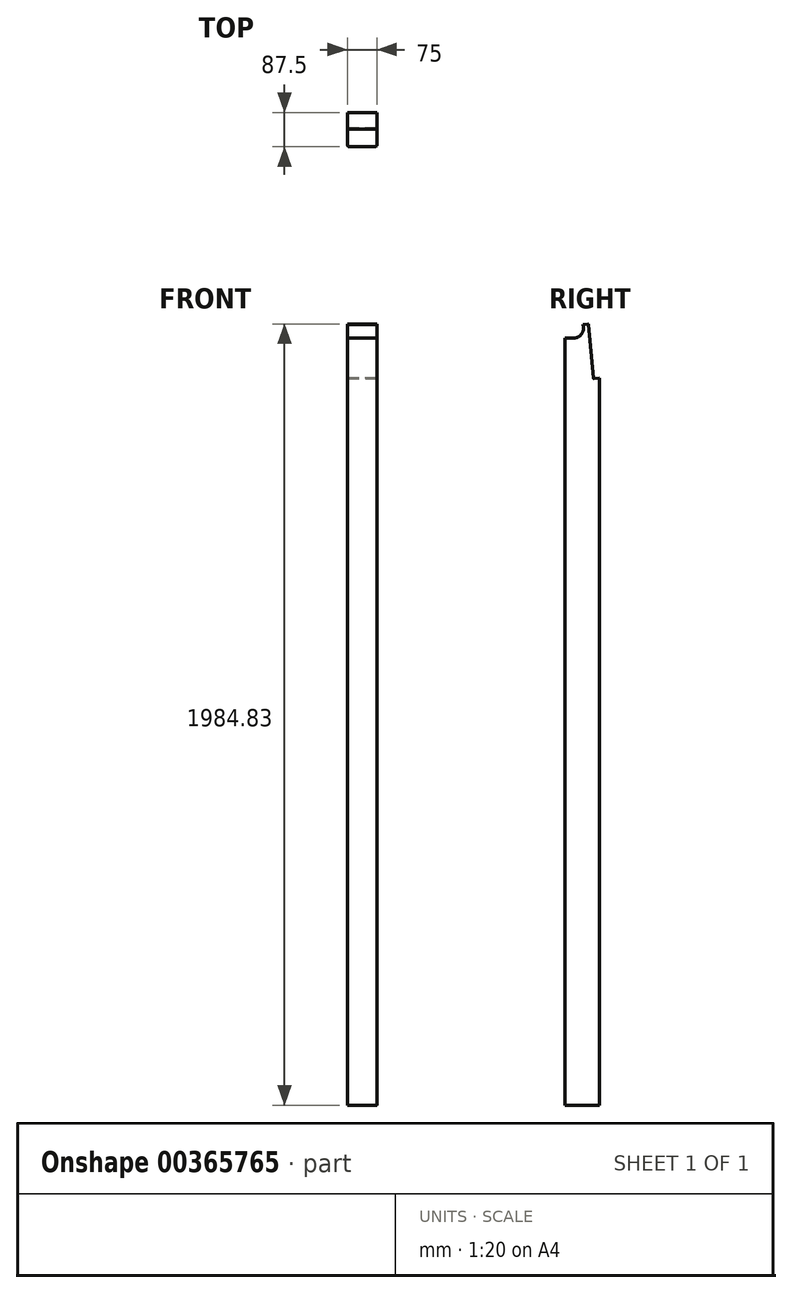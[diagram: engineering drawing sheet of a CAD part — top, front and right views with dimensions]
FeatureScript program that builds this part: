
annotation { "Feature Type Name" : "Feature", "Feature Type Description" : "" }
export const myFeature = defineFeature(function(context is Context, id is Id, definition is map)
    precondition{}
    {
        {
            var Q0;
            Q0=qCreatedBy(makeId("Top.planeOp"),FACE);
            var sketch = newSketch(context, id + "F0", { "sketchPlane" : qUnion([Q0])});
            skLineSegment(sketch, "E0.bottom", {"start": v(-37.5, 43.75) * mm, "end": v(37.5, 43.75) * mm});
            skLineSegment(sketch, "E0.top", {"start": v(-37.5, -43.75) * mm, "end": v(37.5, -43.75) * mm});
            skLineSegment(sketch, "E0.left", {"start": v(-37.5, 43.75) * mm, "end": v(-37.5, -43.75) * mm});
            skLineSegment(sketch, "E0.right", {"start": v(37.5, 43.75) * mm, "end": v(37.5, -43.75) * mm});
            skPoint(sketch, "E0.middle", {"position": v(0, 0) * mm});
            skSolve(sketch);
        }
        {
            var Q0;
            Q0=makeQuery(id+"F0.imprint","IMPRINT",FACE,{"disambiguationData":[TD([[makeQuery(id+"F0.imprint","IMPRINT",EDGE,{"derivedFrom":sQuery(id+"F0.wireOp",EDGE,"E0.bottom")}),-1.0]])]});
            extrude(context, id + "F1", {"entities" : qUnion([Q0]), "depth" : 2000 * mm});
        }
        {
            var Q0;
            Q0=makeQuery(id+"F1.opExtrude","SWEPT_EDGE",EDGE,{"disambiguationData":[OSD([sQuery(id+"F0.wireOp",EDGE,"E0.top"),sQuery(id+"F0.wireOp",EDGE,"E0.left")])]});
            var Q1;
            Q1=makeQuery(id+"F1.opExtrude","SWEPT_EDGE",EDGE,{"disambiguationData":[OSD([sQuery(id+"F0.wireOp",EDGE,"E0.top"),sQuery(id+"F0.wireOp",EDGE,"E0.right")])]});
            fillet(context, id + "F2", {"entities" : qUnion([Q0, Q1]), "radius" : 5 * mm, "tangentPropagation" : true, "allowEdgeOverflow" : false});
        }
        {
            var Q0;
            Q0=makeQuery(id+"F1.opExtrude","SWEPT_FACE",FACE,{"disambiguationData":[OSD([sQuery(id+"F0.wireOp",EDGE,"E0.left")])]});
            var sketch = newSketch(context, id + "F3", { "sketchPlane" : qUnion([Q0])});
            skLineSegment(sketch, "E1", {"start": v(-16.6, 1985) * mm, "end": v(-28.8, 1845.53) * mm});
            skLineSegment(sketch, "E2", {"start": v(-28.8, 1845.53) * mm, "end": v(-43.75, 1846.84) * mm});
            skLineSegment(sketch, "E3", {"start": v(-43.75, 1846.84) * mm, "end": v(-43.75, 2000) * mm});
            skLineSegment(sketch, "E4", {"start": v(-43.75, 2000) * mm, "end": v(43.75, 2000) * mm});
            skLineSegment(sketch, "E5", {"start": v(21.25, 1949) * mm, "end": v(43.75, 1949) * mm});
            skLineSegment(sketch, "E6", {"start": v(43.75, 1949) * mm, "end": v(43.75, 2000) * mm});
            skArc(sketch, "E7", {"start": v(-1.79, 1983.7) * mm, "mid": v(0.42, 1960.17) * mm, "end": v(21.25, 1949) * mm});
            skLineSegment(sketch, "E8", {"start": v(-16.6, 1985) * mm, "end": v(-1.79, 1983.7) * mm});
            skSolve(sketch);
        }
        {
            var Q0;
            Q0=makeQuery(id+"F3.imprint","IMPRINT",FACE,{"disambiguationData":[TD([[makeQuery(id+"F3.imprint","IMPRINT",EDGE,{"derivedFrom":sQuery(id+"F3.wireOp",EDGE,"E1")}),-1.0]])]});
            var Q1;
            {var subQ0=sQuery(id+"F3.wireOp",EDGE,"E4");var subQ4=sQuery(id+"F3.wireOp",EDGE,"urJoZquf-hlon-n6bp-8leZ-iI16e2esaS3W");var subQ5=makeQuery(id+"F3.imprint","INTERSECT",VERTEX,{"derivedFrom":[subQ0,subQ4]});Q1=makeQuery(id+"F3.imprint","IMPRINT",FACE,{"disambiguationData":[TD([[makeQuery(id+"F3.imprint","IMPRINT",EDGE,{"disambiguationData":[TD([[subQ5,1.0]])],"derivedFrom":subQ0}),-1.0]])]});}
            extrude(context, id + "F4", {"entities" : qUnion([Q0, Q1]), "operationType" : NewBodyOperationType.REMOVE, "endBound" : BoundingType.THROUGH_ALL, "oppositeDirection" : true, "depth" : 25 * mm});
        }
        {
            var Q0;
            Q0=makeQuery(id+"F4.boolean.opBoolean","COPY",EDGE,{"derivedFrom":makeQuery(id+"F4.opExtrude","SWEPT_EDGE",EDGE,{"disambiguationData":[OSD([sQuery(id+"F3.wireOp",EDGE,"E1"),sQuery(id+"F3.wireOp",EDGE,"4EJ12AgS-1P0p-YSoj-b53e-VyAeUD9TmmNq")])]})});
            fillet(context, id + "F5", {"entities" : qUnion([Q0]), "radius" : 2 * mm, "tangentPropagation" : true, "allowEdgeOverflow" : false});
        }
    });
